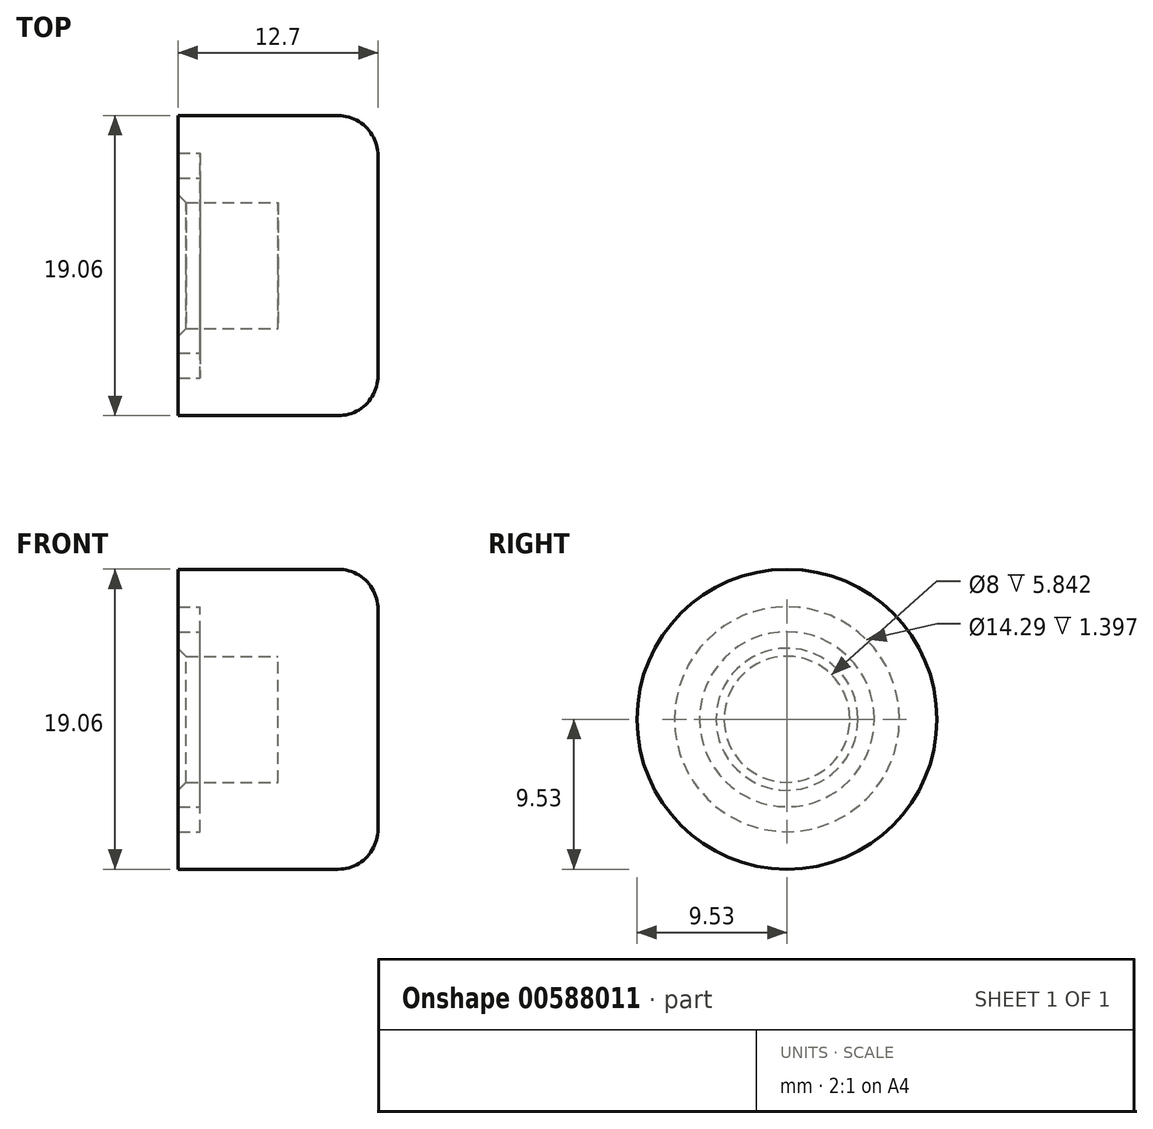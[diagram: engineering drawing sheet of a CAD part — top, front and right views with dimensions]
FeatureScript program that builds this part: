
annotation { "Feature Type Name" : "Feature", "Feature Type Description" : "" }
export const myFeature = defineFeature(function(context is Context, id is Id, definition is map)
    precondition{}
    {
        {
            var Q0;
            Q0=qCreatedBy(makeId("Front.planeOp"),FACE);
            var sketch = newSketch(context, id + "F0", { "sketchPlane" : qUnion([Q0])});
            skLineSegment(sketch, "E0", {"start": v(0, 4) * mm, "end": v(0, 5.56) * mm});
            skLineSegment(sketch, "E1", {"start": v(0, 5.56) * mm, "end": v(1.4, 5.56) * mm});
            skLineSegment(sketch, "E2", {"start": v(1.4, 5.56) * mm, "end": v(1.4, 7.14) * mm});
            skLineSegment(sketch, "E3", {"start": v(1.4, 7.14) * mm, "end": v(0, 7.14) * mm});
            skLineSegment(sketch, "E4", {"start": v(0, 7.14) * mm, "end": v(0, 9.53) * mm});
            skLineSegment(sketch, "E5", {"start": v(0, 9.53) * mm, "end": v(12.7, 9.53) * mm});
            skLineSegment(sketch, "E6", {"start": v(12.7, 9.53) * mm, "end": v(12.7, 0) * mm});
            skLineSegment(sketch, "E7", {"start": v(12.7, 0) * mm, "end": v(6.35, 0) * mm});
            skLineSegment(sketch, "E8", {"start": v(6.35, 0) * mm, "end": v(6.35, 4) * mm});
            skLineSegment(sketch, "E9", {"start": v(6.35, 4) * mm, "end": v(0, 4) * mm});
            skSolve(sketch);
        }
        {
            var Q0;
            Q0=makeQuery(id+"F0.imprint","IMPRINT",FACE,{"disambiguationData":[TD([[makeQuery(id+"F0.imprint","IMPRINT",EDGE,{"derivedFrom":sQuery(id+"F0.wireOp",EDGE,"E0")}),-1.0]])]});
            var Q1;
            Q1=sQuery(id+"F0.wireOp",EDGE,"E7");
            revolve(context, id + "F1", {"surfaceOperationType" : NewSurfaceOperationType.NEW, "entities" : qUnion([Q0]), "axis" : qUnion([Q1]), "revolveType" : RevolveType.FULL});
        }
        {
            var Q0;
            Q0=makeQuery(id+"F1.opRevolve","SWEPT_EDGE",EDGE,{"disambiguationData":[OSD([sQuery(id+"F0.wireOp",EDGE,"E0"),sQuery(id+"F0.wireOp",EDGE,"E9")])]});
            chamfer(context, id + "F2", {"entities" : qUnion([Q0]), "width" : 0.5 * mm, "tangentPropagation" : true});
        }
        {
            var Q0;
            Q0=makeQuery(id+"F1.opRevolve","SWEPT_EDGE",EDGE,{"disambiguationData":[OSD([sQuery(id+"F0.wireOp",EDGE,"E5"),sQuery(id+"F0.wireOp",EDGE,"E6")])]});
            fillet(context, id + "F3", {"entities" : qUnion([Q0]), "tangentPropagation" : true, "radius" : 2.54 * mm, "defaultsChanged" : true, "vertexSettings" : [], "allowEdgeOverflow" : false});
        }
    });
